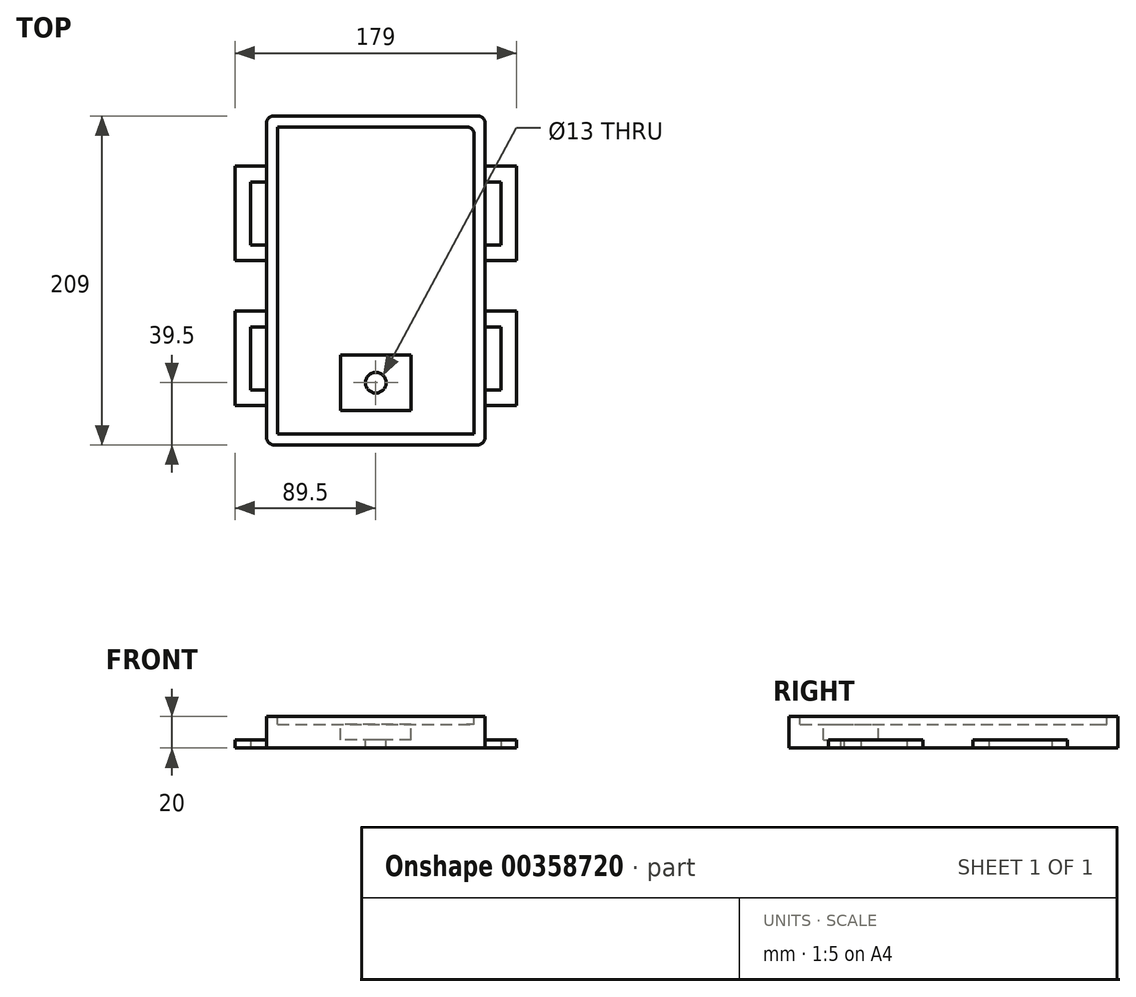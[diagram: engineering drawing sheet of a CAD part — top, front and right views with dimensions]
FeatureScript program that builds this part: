
annotation { "Feature Type Name" : "Feature", "Feature Type Description" : "" }
export const myFeature = defineFeature(function(context is Context, id is Id, definition is map)
    precondition{}
    {
        {
            var Q0;
            Q0=qCreatedBy(makeId("Top.planeOp"),FACE);
            var sketch = newSketch(context, id + "F0", { "sketchPlane" : qUnion([Q0])});
            skLineSegment(sketch, "E0.bottom", {"start": v(0, 0) * mm, "end": v(125, 0) * mm});
            skLineSegment(sketch, "E0.top", {"start": v(0, 195) * mm, "end": v(125, 195) * mm});
            skLineSegment(sketch, "E0.left", {"start": v(0, 0) * mm, "end": v(0, 195) * mm});
            skLineSegment(sketch, "E0.right", {"start": v(125, 0) * mm, "end": v(125, 195) * mm});
            skLineSegment(sketch, "E1.0", {"start": v(-7, 202) * mm, "end": v(132, 202) * mm});
            skLineSegment(sketch, "E1.1", {"start": v(-7, -7) * mm, "end": v(-7, 202) * mm});
            skLineSegment(sketch, "E1.2", {"start": v(-7, -7) * mm, "end": v(132, -7) * mm});
            skLineSegment(sketch, "E1.3", {"start": v(132, -7) * mm, "end": v(132, 202) * mm});
            skSolve(sketch);
        }
        {
            var Q0;
            Q0=makeQuery(id+"F0.imprint","IMPRINT",FACE,{"disambiguationData":[TD([[makeQuery(id+"F0.imprint","IMPRINT",EDGE,{"derivedFrom":sQuery(id+"F0.wireOp",EDGE,"E0.bottom")}),1.0]])]});
            var Q1;
            Q1=makeQuery(id+"F0.imprint","IMPRINT",FACE,{"disambiguationData":[TD([[makeQuery(id+"F0.imprint","IMPRINT",EDGE,{"derivedFrom":sQuery(id+"F0.wireOp",EDGE,"E0.bottom")}),-1.0]])]});
            extrude(context, id + "F1", {"entities" : qUnion([Q0, Q1]), "oppositeDirection" : true, "depth" : 20 * mm});
        }
        {
            var Q0;
            Q0=makeQuery(id+"F0.imprint","IMPRINT",FACE,{"disambiguationData":[TD([[makeQuery(id+"F0.imprint","IMPRINT",EDGE,{"derivedFrom":sQuery(id+"F0.wireOp",EDGE,"E0.bottom")}),1.0]])]});
            extrude(context, id + "F2", {"entities" : qUnion([Q0]), "operationType" : NewBodyOperationType.REMOVE, "oppositeDirection" : true, "depth" : 5 * mm});
        }
        {
            var Q0;
            Q0=makeQuery(id+"F0.imprint","IMPRINT",FACE,{"disambiguationData":[TD([[makeQuery(id+"F0.imprint","IMPRINT",EDGE,{"derivedFrom":sQuery(id+"F0.wireOp",EDGE,"E0.bottom")}),1.0]])]});
            var sketch = newSketch(context, id + "F3", { "sketchPlane" : qUnion([Q0])});
            skLineSegment(sketch, "E2.bottom", {"start": v(85, 15) * mm, "end": v(40, 15) * mm});
            skLineSegment(sketch, "E2.top", {"start": v(85, 50) * mm, "end": v(40, 50) * mm});
            skLineSegment(sketch, "E2.left", {"start": v(85, 15) * mm, "end": v(85, 50) * mm});
            skLineSegment(sketch, "E2.right", {"start": v(40, 15) * mm, "end": v(40, 50) * mm});
            skSolve(sketch);
        }
        {
            var Q0;
            Q0 = qSketchRegion(id + "F3", true);
            extrude(context, id + "F4", {"entities" : qUnion([Q0]), "operationType" : NewBodyOperationType.REMOVE, "oppositeDirection" : true, "depth" : 15 * mm});
        }
        {
            var Q0;
            Q0=makeQuery(id+"F0.imprint","IMPRINT",FACE,{"disambiguationData":[TD([[makeQuery(id+"F0.imprint","IMPRINT",EDGE,{"derivedFrom":sQuery(id+"F0.wireOp",EDGE,"E0.bottom")}),1.0]])]});
            var sketch = newSketch(context, id + "F5", { "sketchPlane" : qUnion([Q0])});
            skCircle(sketch, "E3", {"center": v(62.5, 32.5) * mm, "radius": 6.5 * mm});
            skSolve(sketch);
        }
        {
            var Q0;
            Q0 = qSketchRegion(id + "F5", true);
            extrude(context, id + "F6", {"entities" : qUnion([Q0]), "operationType" : NewBodyOperationType.REMOVE, "oppositeDirection" : true, "depth" : 25 * mm});
        }
        {
            var Q0;
            Q0=makeQuery(id+"F1.opExtrude","SWEPT_EDGE",EDGE,{"disambiguationData":[OSD([sQuery(id+"F0.wireOp",EDGE,"E1.1"),sQuery(id+"F0.wireOp",EDGE,"E1.2")])]});
            var Q1;
            Q1=makeQuery(id+"F2.boolean.opBoolean","COPY",EDGE,{"derivedFrom":makeQuery(id+"F2.opExtrude","SWEPT_EDGE",EDGE,{"disambiguationData":[OSD([sQuery(id+"F0.wireOp",EDGE,"E0.top"),sQuery(id+"F0.wireOp",EDGE,"E0.right")])]})});
            var Q2;
            Q2=makeQuery(id+"F1.opExtrude","SWEPT_EDGE",EDGE,{"disambiguationData":[OSD([sQuery(id+"F0.wireOp",EDGE,"E1.0"),sQuery(id+"F0.wireOp",EDGE,"E1.1")])]});
            var Q3;
            Q3=makeQuery(id+"F1.opExtrude","SWEPT_EDGE",EDGE,{"disambiguationData":[OSD([sQuery(id+"F0.wireOp",EDGE,"E1.2"),sQuery(id+"F0.wireOp",EDGE,"E1.3")])]});
            var Q4;
            Q4=makeQuery(id+"F1.opExtrude","SWEPT_EDGE",EDGE,{"disambiguationData":[OSD([sQuery(id+"F0.wireOp",EDGE,"E1.0"),sQuery(id+"F0.wireOp",EDGE,"E1.3")])]});
            fillet(context, id + "F7", {"entities" : qUnion([Q0, Q1, Q2, Q3, Q4]), "radius" : 5 * mm, "tangentPropagation" : true, "allowEdgeOverflow" : false});
        }
        {
            var Q0;
            Q0=makeQuery(id+"F1.opExtrude","CAP_FACE",FACE,{"disambiguationData":[OSD([sQuery(id+"F0.wireOp",EDGE,"E1.0"),sQuery(id+"F0.wireOp",EDGE,"E1.1"),sQuery(id+"F0.wireOp",EDGE,"E1.2"),sQuery(id+"F0.wireOp",EDGE,"E1.3")])],"isStart":false});
            var sketch = newSketch(context, id + "F8", { "sketchPlane" : qUnion([Q0])});
            skLineSegment(sketch, "E4.bottom", {"start": v(152, -170) * mm, "end": v(132, -170) * mm});
            skLineSegment(sketch, "E4.top", {"start": v(152, -110) * mm, "end": v(132, -110) * mm});
            skLineSegment(sketch, "E4.left", {"start": v(152, -170) * mm, "end": v(152, -110) * mm});
            skLineSegment(sketch, "E4.right", {"start": v(-27, -170) * mm, "end": v(-27, -110) * mm});
            skLineSegment(sketch, "E5.bottom", {"start": v(152, -78) * mm, "end": v(132, -78) * mm});
            skLineSegment(sketch, "E5.top", {"start": v(152, -18) * mm, "end": v(132, -18) * mm});
            skLineSegment(sketch, "E5.left", {"start": v(152, -78) * mm, "end": v(152, -18) * mm});
            skLineSegment(sketch, "E5.right", {"start": v(-27, -78) * mm, "end": v(-27, -18) * mm});
            skLineSegment(sketch, "E6.0", {"start": v(-17, -68) * mm, "end": v(-17, -28) * mm});
            skLineSegment(sketch, "E6.1", {"start": v(142, -68) * mm, "end": v(132, -68) * mm});
            skLineSegment(sketch, "E6.2", {"start": v(142, -68) * mm, "end": v(142, -28) * mm});
            skLineSegment(sketch, "E6.3", {"start": v(142, -28) * mm, "end": v(132, -28) * mm});
            skLineSegment(sketch, "E7.left", {"start": v(-7, -18) * mm, "end": v(-7, -28) * mm});
            skLineSegment(sketch, "E7.right", {"start": v(132, -18) * mm, "end": v(132, -28) * mm});
            skLineSegment(sketch, "E8.0", {"start": v(142, -120) * mm, "end": v(132, -120) * mm});
            skLineSegment(sketch, "E8.1", {"start": v(142, -160) * mm, "end": v(142, -120) * mm});
            skLineSegment(sketch, "E8.2", {"start": v(142, -160) * mm, "end": v(132, -160) * mm});
            skLineSegment(sketch, "E8.3", {"start": v(-17, -160) * mm, "end": v(-17, -120) * mm});
            skLineSegment(sketch, "E9.trimOffspring", {"start": v(-7, -18) * mm, "end": v(-27, -18) * mm});
            skLineSegment(sketch, "E10.trimOffspring", {"start": v(-7, -28) * mm, "end": v(-17, -28) * mm});
            skLineSegment(sketch, "E11.trimOffspring", {"start": v(-7, -68) * mm, "end": v(-17, -68) * mm});
            skLineSegment(sketch, "E12.trimOffspring", {"start": v(-7, -78) * mm, "end": v(-27, -78) * mm});
            skLineSegment(sketch, "E13.trimOffspring", {"start": v(-7, -110) * mm, "end": v(-27, -110) * mm});
            skLineSegment(sketch, "E14.trimOffspring", {"start": v(-7, -120) * mm, "end": v(-17, -120) * mm});
            skLineSegment(sketch, "E15.trimOffspring", {"start": v(-7, -160) * mm, "end": v(-17, -160) * mm});
            skLineSegment(sketch, "E16.trimOffspring", {"start": v(-7, -170) * mm, "end": v(-27, -170) * mm});
            skLineSegment(sketch, "E17.trimOffspring", {"start": v(-7, -68) * mm, "end": v(-7, -78) * mm});
            skLineSegment(sketch, "E18.trimOffspring", {"start": v(132, -68) * mm, "end": v(132, -78) * mm});
            skLineSegment(sketch, "E19.trimOffspring", {"start": v(132, -110) * mm, "end": v(132, -170) * mm});
            skLineSegment(sketch, "E20.trimOffspring", {"start": v(-7, -110) * mm, "end": v(-7, -170) * mm});
            skSolve(sketch);
        }
        {
            var Q0;
            Q0=makeQuery(id+"F8.imprint","IMPRINT",FACE,{"disambiguationData":[TD([[makeQuery(id+"F8.imprint","IMPRINT",EDGE,{"derivedFrom":sQuery(id+"F8.wireOp",EDGE,"E4.right")}),-1.0]])]});
            var Q1;
            Q1=makeQuery(id+"F8.imprint","IMPRINT",FACE,{"disambiguationData":[TD([[makeQuery(id+"F8.imprint","IMPRINT",EDGE,{"derivedFrom":sQuery(id+"F8.wireOp",EDGE,"E5.right")}),-1.0]])]});
            var Q2;
            Q2=makeQuery(id+"F8.imprint","IMPRINT",FACE,{"disambiguationData":[TD([[makeQuery(id+"F8.imprint","IMPRINT",EDGE,{"derivedFrom":sQuery(id+"F8.wireOp",EDGE,"E5.bottom")}),-1.0]])]});
            var Q3;
            {var subQ2=sQuery(id+"F8.wireOp",EDGE,"E4.bottom");Q3=makeQuery(id+"F8.imprint","IMPRINT",FACE,{"disambiguationData":[TD([[makeQuery(id+"F8.imprint","IMPRINT",EDGE,{"derivedFrom":subQ2}),-1.0]])]});}
            extrude(context, id + "F9", {"entities" : qUnion([Q0, Q1, Q2, Q3]), "operationType" : NewBodyOperationType.ADD, "oppositeDirection" : true, "depth" : 5 * mm});
        }
    });
